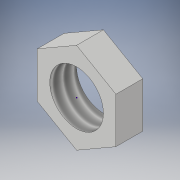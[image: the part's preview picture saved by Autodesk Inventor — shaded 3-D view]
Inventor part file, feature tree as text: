
AUTODESK INVENTOR PART (.ipt)
format: ipt  version: 2017 (Build 210142000, 142)  size: 104,448 bytes
history: native  units: in
note: dims shown in document units (in); Inventor stores cm internally (conversion verified against a paired STEP export)
features: sketch x2, extrude x1, thread x1
ambient origin geometry x8: Origin, YZ Plane, XZ Plane, XY Plane, X Axis, Y Axis, Z Axis, Center Point
bodies: Solid1 (feature_tree)
feature tree (4):
  extrude  "Extrusion1"  Depth=0.0625in TaperAngle=0.0deg
  sketch  "Sketch2"
  thread  "Thread1"  [1 undecoded]
  sketch  "Sketch1"  dims[d0=0.125in d1=0.0625in d2=0.0in d3=1.0in d4=0.0in]
note: 1 required parameter value undecoded (feature->parameter linkage not recoverable at this tier; creation-order binding heuristic only, values carry confidence <= 0.55)
